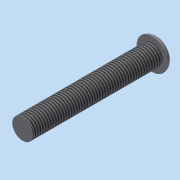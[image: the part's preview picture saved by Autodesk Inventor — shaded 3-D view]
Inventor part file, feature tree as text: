
AUTODESK INVENTOR PART (.ipt)
format: ipt  version: 2015 (Build 190159000, 159)  size: 96,256 bytes
history: native  units: mm
features: revolve x1, fillet x1, thread x1, sketch x1
ambient origin geometry x8: Origin, YZ Plane, XZ Plane, XY Plane, X Axis, Y Axis, Z Axis, Center Point
bodies: Solid1 (feature_tree)
feature tree (4):
  revolve  "Revolution1"  [1 undecoded]
  fillet  "Fillet1"  Radius=1.0mm
  thread  "Thread1"  [1 undecoded]
  sketch  "Sketch1"  dims[d0=2.0mm d1=3.0mm d2=1.0mm d3=90.0deg d4=1.0mm d5=10.0mm d6=0.0mm d7=25.0mm]
note: 2 required parameter values undecoded (feature->parameter linkage not recoverable at this tier; creation-order binding heuristic only, values carry confidence <= 0.55)